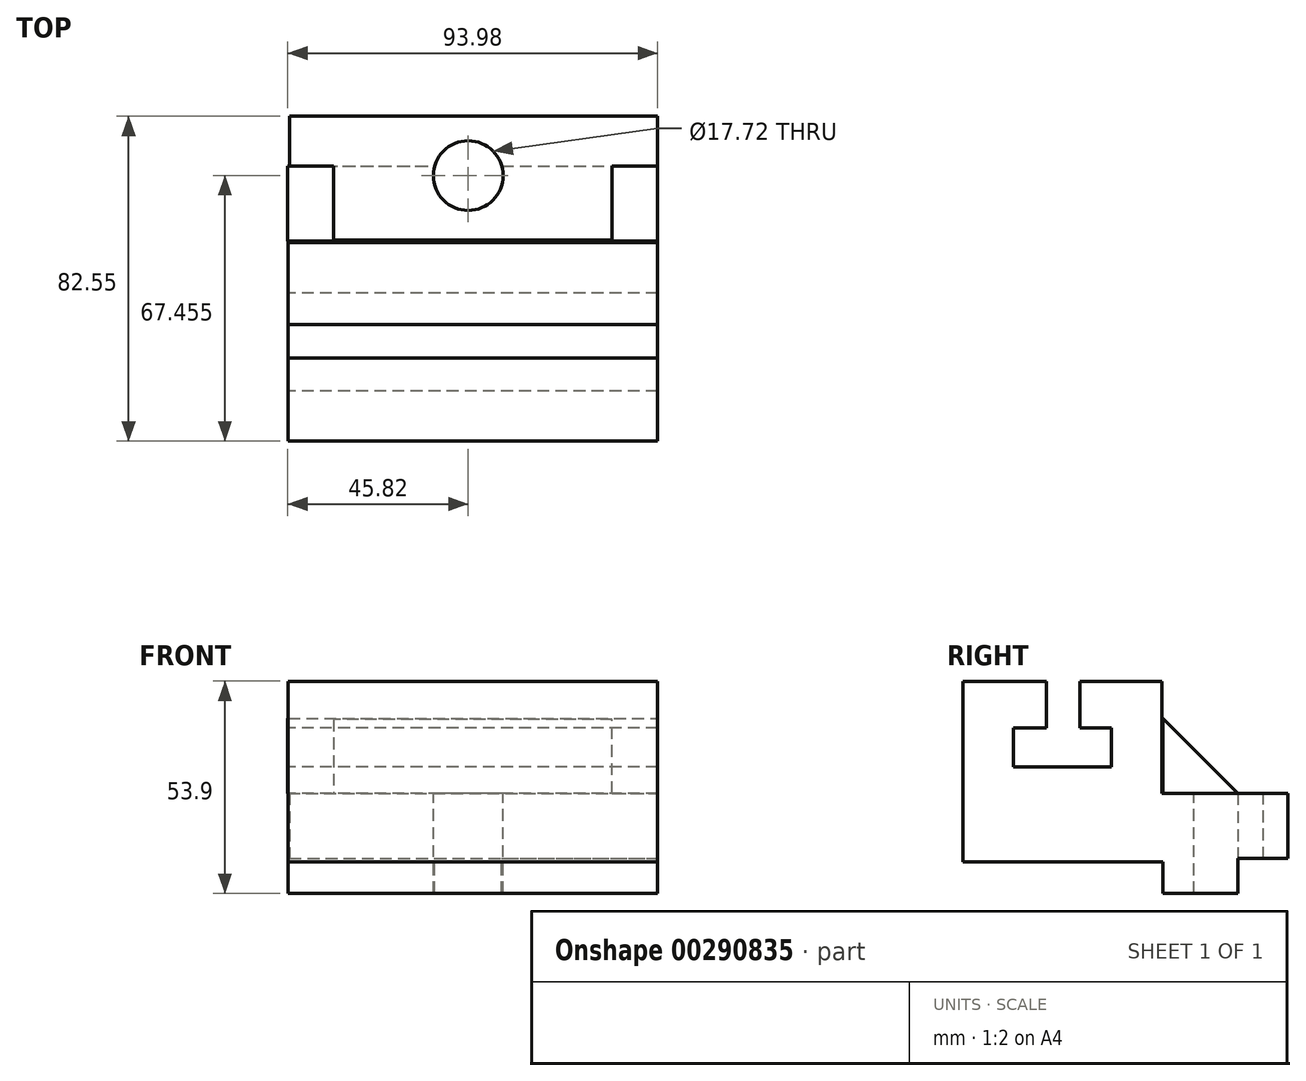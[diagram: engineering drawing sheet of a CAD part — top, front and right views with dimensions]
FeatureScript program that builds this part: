
annotation { "Feature Type Name" : "Feature", "Feature Type Description" : "" }
export const myFeature = defineFeature(function(context is Context, id is Id, definition is map)
    precondition{}
    {
        {
            var Q0;
            Q0=qCreatedBy(makeId("Front.planeOp"),FACE);
            var sketch = newSketch(context, id + "F0", { "sketchPlane" : qUnion([Q0])});
            skLineSegment(sketch, "E0", {"start": v(-45.72, 0) * mm, "end": v(-45.72, -25.45) * mm});
            skLineSegment(sketch, "E1", {"start": v(-45.72, -25.45) * mm, "end": v(48.16, -25.45) * mm});
            skLineSegment(sketch, "E2", {"start": v(48.16, -25.45) * mm, "end": v(48.16, 0) * mm});
            skLineSegment(sketch, "E3", {"start": v(48.16, 0) * mm, "end": v(-45.72, 0) * mm});
            skSolve(sketch);
        }
        {
            var Q0;
            Q0=makeQuery(id+"F0.imprint","IMPRINT",FACE,{"disambiguationData":[TD([[makeQuery(id+"F0.imprint","IMPRINT",EDGE,{"derivedFrom":sQuery(id+"F0.wireOp",EDGE,"E0")}),1.0]])]});
            extrude(context, id + "F1", {"entities" : qUnion([Q0]), "depth" : 19.05 * mm});
        }
        {
            var Q0;
            Q0=qCreatedBy(makeId("Front.planeOp"),FACE);
            var sketch = newSketch(context, id + "F2", { "sketchPlane" : qUnion([Q0])});
            skLineSegment(sketch, "E4", {"start": v(48.16, -16.61) * mm, "end": v(48.16, 0) * mm});
            skLineSegment(sketch, "E5", {"start": v(48.16, 0) * mm, "end": v(-45.42, 0) * mm});
            skLineSegment(sketch, "E6", {"start": v(-45.42, 0) * mm, "end": v(-45.42, -16.61) * mm});
            skLineSegment(sketch, "E7", {"start": v(-45.42, -16.61) * mm, "end": v(48.16, -16.61) * mm});
            skSolve(sketch);
        }
        {
            var Q0;
            Q0=makeQuery(id+"F2.imprint","IMPRINT",FACE,{"disambiguationData":[TD([[makeQuery(id+"F2.imprint","IMPRINT",EDGE,{"derivedFrom":sQuery(id+"F2.wireOp",EDGE,"E4")}),1.0]])]});
            extrude(context, id + "F3", {"entities" : qUnion([Q0]), "operationType" : NewBodyOperationType.ADD, "oppositeDirection" : true, "depth" : 12.7 * mm});
        }
        {
            var Q0;
            Q0=makeQuery(id+"F1.opExtrude","CAP_FACE",FACE,{"disambiguationData":[OSD([sQuery(id+"F0.wireOp",EDGE,"E0"),sQuery(id+"F0.wireOp",EDGE,"E1"),sQuery(id+"F0.wireOp",EDGE,"E2"),sQuery(id+"F0.wireOp",EDGE,"E3")])],"isStart":false});
            var sketch = newSketch(context, id + "F4", { "sketchPlane" : qUnion([Q0])});
            skLineSegment(sketch, "E8", {"start": v(-45.72, -17.45) * mm, "end": v(48.16, -17.45) * mm});
            skLineSegment(sketch, "E9", {"start": v(48.16, -17.45) * mm, "end": v(48.16, 0) * mm});
            skLineSegment(sketch, "E10", {"start": v(48.16, 0) * mm, "end": v(-45.72, 0) * mm});
            skLineSegment(sketch, "E11", {"start": v(-45.72, 0) * mm, "end": v(-45.72, -17.45) * mm});
            skSolve(sketch);
        }
        {
            var Q0;
            Q0=makeQuery(id+"F4.imprint","IMPRINT",FACE,{"disambiguationData":[TD([[makeQuery(id+"F4.imprint","IMPRINT",EDGE,{"derivedFrom":sQuery(id+"F4.wireOp",EDGE,"E8")}),1.0]])]});
            extrude(context, id + "F5", {"entities" : qUnion([Q0]), "operationType" : NewBodyOperationType.ADD, "depth" : 50.8 * mm});
        }
        {
            var Q0;
            Q0=makeQuery(id+"F5.boolean.opBoolean","MERGE",FACE,{"derivedFrom":[makeQuery(id+"F3.boolean.opBoolean","MERGE",FACE,{"derivedFrom":[makeQuery(id+"F1.opExtrude","SWEPT_FACE",FACE,{"disambiguationData":[OSD([sQuery(id+"F0.wireOp",EDGE,"E2")])]}),makeQuery(id+"F3.opExtrude","SWEPT_FACE",FACE,{"disambiguationData":[OSD([sQuery(id+"F2.wireOp",EDGE,"E4")])]})]}),makeQuery(id+"F5.opExtrude","SWEPT_FACE",FACE,{"disambiguationData":[OSD([sQuery(id+"F4.wireOp",EDGE,"E9")])]})]});
            var sketch = newSketch(context, id + "F6", { "sketchPlane" : qUnion([Q0])});
            skLineSegment(sketch, "E12", {"start": v(-19.05, 0) * mm, "end": v(-19.05, 19.05) * mm});
            skLineSegment(sketch, "E13", {"start": v(-19.05, 19.05) * mm, "end": v(0, 0) * mm});
            skLineSegment(sketch, "E14", {"start": v(0, 0) * mm, "end": v(-19.05, 0) * mm});
            skSolve(sketch);
        }
        {
            var Q0;
            Q0=makeQuery(id+"F6.imprint","IMPRINT",FACE,{"disambiguationData":[TD([[makeQuery(id+"F6.imprint","IMPRINT",EDGE,{"derivedFrom":sQuery(id+"F6.wireOp",EDGE,"E12")}),-1.0]])]});
            extrude(context, id + "F7", {"entities" : qUnion([Q0]), "oppositeDirection" : true, "depth" : 93.98 * mm});
        }
        {
            var Q0;
            Q0=makeQuery(id+"F3.opExtrude","CAP_FACE",FACE,{"disambiguationData":[OSD([sQuery(id+"F2.wireOp",EDGE,"E4"),sQuery(id+"F2.wireOp",EDGE,"E5"),sQuery(id+"F2.wireOp",EDGE,"E6"),sQuery(id+"F2.wireOp",EDGE,"E7")])],"isStart":false});
            var sketch = newSketch(context, id + "F8", { "sketchPlane" : qUnion([Q0])});
            skLineSegment(sketch, "E15", {"start": v(-36.58, 0) * mm, "end": v(-36.58, 18.75) * mm});
            skLineSegment(sketch, "E16", {"start": v(-36.58, 18.75) * mm, "end": v(34.14, 18.75) * mm});
            skLineSegment(sketch, "E17", {"start": v(34.14, 18.75) * mm, "end": v(34.14, 0) * mm});
            skLineSegment(sketch, "E18", {"start": v(34.14, 0) * mm, "end": v(-36.58, 0) * mm});
            skSolve(sketch);
        }
        {
            var Q0;
            Q0 = qSketchRegion(id + "F8", true);
            extrude(context, id + "F9", {"entities" : qUnion([Q0]), "operationType" : NewBodyOperationType.REMOVE, "oppositeDirection" : true, "depth" : 115.82 * mm});
        }
        {
            var Q0;
            Q0 = qSketchRegion(id + "F8", true);
            extrude(context, id + "F10", {"entities" : qUnion([Q0]), "operationType" : NewBodyOperationType.REMOVE, "oppositeDirection" : true, "depth" : 152.4 * mm});
        }
        {
            var Q0;
            Q0 = qSketchRegion(id + "F8", true);
            extrude(context, id + "F11", {"entities" : qUnion([Q0]), "operationType" : NewBodyOperationType.REMOVE, "oppositeDirection" : true, "depth" : 194.82 * mm});
        }
        {
            var Q0;
            Q0=makeQuery(id+"F5.boolean.opBoolean","MERGE",FACE,{"derivedFrom":[makeQuery(id+"F3.boolean.opBoolean","MERGE",FACE,{"derivedFrom":[makeQuery(id+"F1.opExtrude","SWEPT_FACE",FACE,{"disambiguationData":[OSD([sQuery(id+"F0.wireOp",EDGE,"E3")])]}),makeQuery(id+"F3.opExtrude","SWEPT_FACE",FACE,{"disambiguationData":[OSD([sQuery(id+"F2.wireOp",EDGE,"E5")])]})]}),makeQuery(id+"F5.opExtrude","SWEPT_FACE",FACE,{"disambiguationData":[OSD([sQuery(id+"F4.wireOp",EDGE,"E10")])]})]});
            var sketch = newSketch(context, id + "F12", { "sketchPlane" : qUnion([Q0])});
            skLineSegment(sketch, "E19", {"start": v(-45.72, -19.35) * mm, "end": v(48.16, -19.35) * mm});
            skLineSegment(sketch, "E20", {"start": v(48.16, -19.35) * mm, "end": v(48.16, -69.85) * mm});
            skLineSegment(sketch, "E21", {"start": v(48.16, -69.85) * mm, "end": v(-45.72, -69.85) * mm});
            skLineSegment(sketch, "E22", {"start": v(-45.72, -69.85) * mm, "end": v(-45.72, -19.35) * mm});
            skSolve(sketch);
        }
        {
            var Q0;
            Q0 = qSketchRegion(id + "F12", true);
            extrude(context, id + "F13", {"entities" : qUnion([Q0]), "operationType" : NewBodyOperationType.ADD, "depth" : 28.45 * mm});
        }
        {
            var Q0;
            Q0=makeQuery(id+"F13.boolean.opBoolean","MERGE",FACE,{"derivedFrom":[makeQuery(id+"F5.boolean.opBoolean","MERGE",FACE,{"derivedFrom":[makeQuery(id+"F1.opExtrude","SWEPT_FACE",FACE,{"disambiguationData":[OSD([sQuery(id+"F0.wireOp",EDGE,"E0")])]}),makeQuery(id+"F5.opExtrude","SWEPT_FACE",FACE,{"disambiguationData":[OSD([sQuery(id+"F4.wireOp",EDGE,"E11")])]})]}),makeQuery(id+"F13.opExtrude","SWEPT_FACE",FACE,{"disambiguationData":[OSD([sQuery(id+"F12.wireOp",EDGE,"E22")])]})]});
            var sketch = newSketch(context, id + "F14", { "sketchPlane" : qUnion([Q0])});
            skLineSegment(sketch, "E23", {"start": v(32.18, 6.7) * mm, "end": v(57.08, 6.7) * mm});
            skLineSegment(sketch, "E24", {"start": v(57.08, 6.7) * mm, "end": v(57.08, 16.63) * mm});
            skLineSegment(sketch, "E25", {"start": v(57.08, 16.63) * mm, "end": v(48.72, 16.63) * mm});
            skLineSegment(sketch, "E26", {"start": v(48.72, 16.63) * mm, "end": v(48.72, 28.45) * mm});
            skLineSegment(sketch, "E27", {"start": v(48.72, 28.45) * mm, "end": v(48.72, 16.63) * mm});
            skLineSegment(sketch, "E28", {"start": v(32.18, 6.7) * mm, "end": v(32.18, 16.63) * mm});
            skLineSegment(sketch, "E29", {"start": v(32.18, 16.63) * mm, "end": v(40.2, 16.63) * mm});
            skLineSegment(sketch, "E30", {"start": v(40.2, 16.63) * mm, "end": v(40.2, 28.45) * mm});
            skLineSegment(sketch, "E31", {"start": v(40.2, 28.45) * mm, "end": v(40.2, 16.63) * mm});
            skSolve(sketch);
        }
        {
            var Q0;
            Q0 = qSketchRegion(id + "F14", true);
            var Q1;
            Q1=makeQuery(id+"F14.imprint","IMPRINT",FACE,{"disambiguationData":[TD([[makeQuery(id+"F14.imprint","IMPRINT",EDGE,{"derivedFrom":sQuery(id+"F14.wireOp",EDGE,"E23")}),1.0]])]});
            extrude(context, id + "F15", {"entities" : qUnion([Q0, Q1]), "operationType" : NewBodyOperationType.REMOVE, "oppositeDirection" : true, "depth" : 177.8 * mm});
        }
        {
            var Q0;
            Q0=makeQuery(id+"F5.boolean.opBoolean","MERGE",FACE,{"derivedFrom":[makeQuery(id+"F3.boolean.opBoolean","MERGE",FACE,{"derivedFrom":[makeQuery(id+"F1.opExtrude","SWEPT_FACE",FACE,{"disambiguationData":[OSD([sQuery(id+"F0.wireOp",EDGE,"E3")])]}),makeQuery(id+"F3.opExtrude","SWEPT_FACE",FACE,{"disambiguationData":[OSD([sQuery(id+"F2.wireOp",EDGE,"E5")])]})]}),makeQuery(id+"F5.opExtrude","SWEPT_FACE",FACE,{"disambiguationData":[OSD([sQuery(id+"F4.wireOp",EDGE,"E10")])]})]});
            var sketch = newSketch(context, id + "F16", { "sketchPlane" : qUnion([Q0])});
            skCircle(sketch, "E32", {"center": v(0, -2.4) * mm, "radius": 8.86 * mm});
            skSolve(sketch);
        }
        {
            var Q0;
            Q0=makeQuery(id+"F16.imprint","IMPRINT",FACE,{"disambiguationData":[TD([[makeQuery(id+"F16.imprint","IMPRINT",EDGE,{"derivedFrom":sQuery(id+"F16.wireOp",EDGE,"E32")}),1.0]])]});
            extrude(context, id + "F17", {"entities" : qUnion([Q0]), "operationType" : NewBodyOperationType.REMOVE, "oppositeDirection" : true, "depth" : 127 * mm});
        }
    });
